# Revit family: Concealed Cistern - Back to Wall Pans
name_source: partatom
category: Plumbing Fixtures
units: mm (PartAtom-declared; Revit-internal decimal feet)

## family parameters
Always vertical = Yes
Cut with Voids When Loaded = No
Enable Cutting in Views = No
Host = Wall
Maintain Annotation Orientation = No
OmniClass Number = 23.45.00.00
OmniClass Title = Sanitary, Laundry, and Cleaning Equipment
Part Type = Normal
Room Calculation Point = No
Round Connector Dimension = Use Diameter
Shared = No

## types (1)
- Concealed Cistern - Back to Wall Pans
    Brackets = Steel
    Category = Concealed Cisterns
    Default Elevation = 0 mm  [stored 0 ft]
    Drainage = PVC
    Manufacturer = Lecico SA
    Material = HDPE (High-Density Polyethylene
    Model = Concealed Cistern - Back to Wall Pans
    Product Code = LECCONCISBTW0BC
    Tank = Plastic
    Technical Dimensions = W460 x H545 x D93mm
    URL = https://www.lecicosa.co.za

note: [stored X ft] marks values corroborated as IEEE doubles in the binary element streams (Revit-internal decimal feet)

## geometry (parser evidence)
native form markers: Sweep x4
no freeform markers — native parametric forms only
